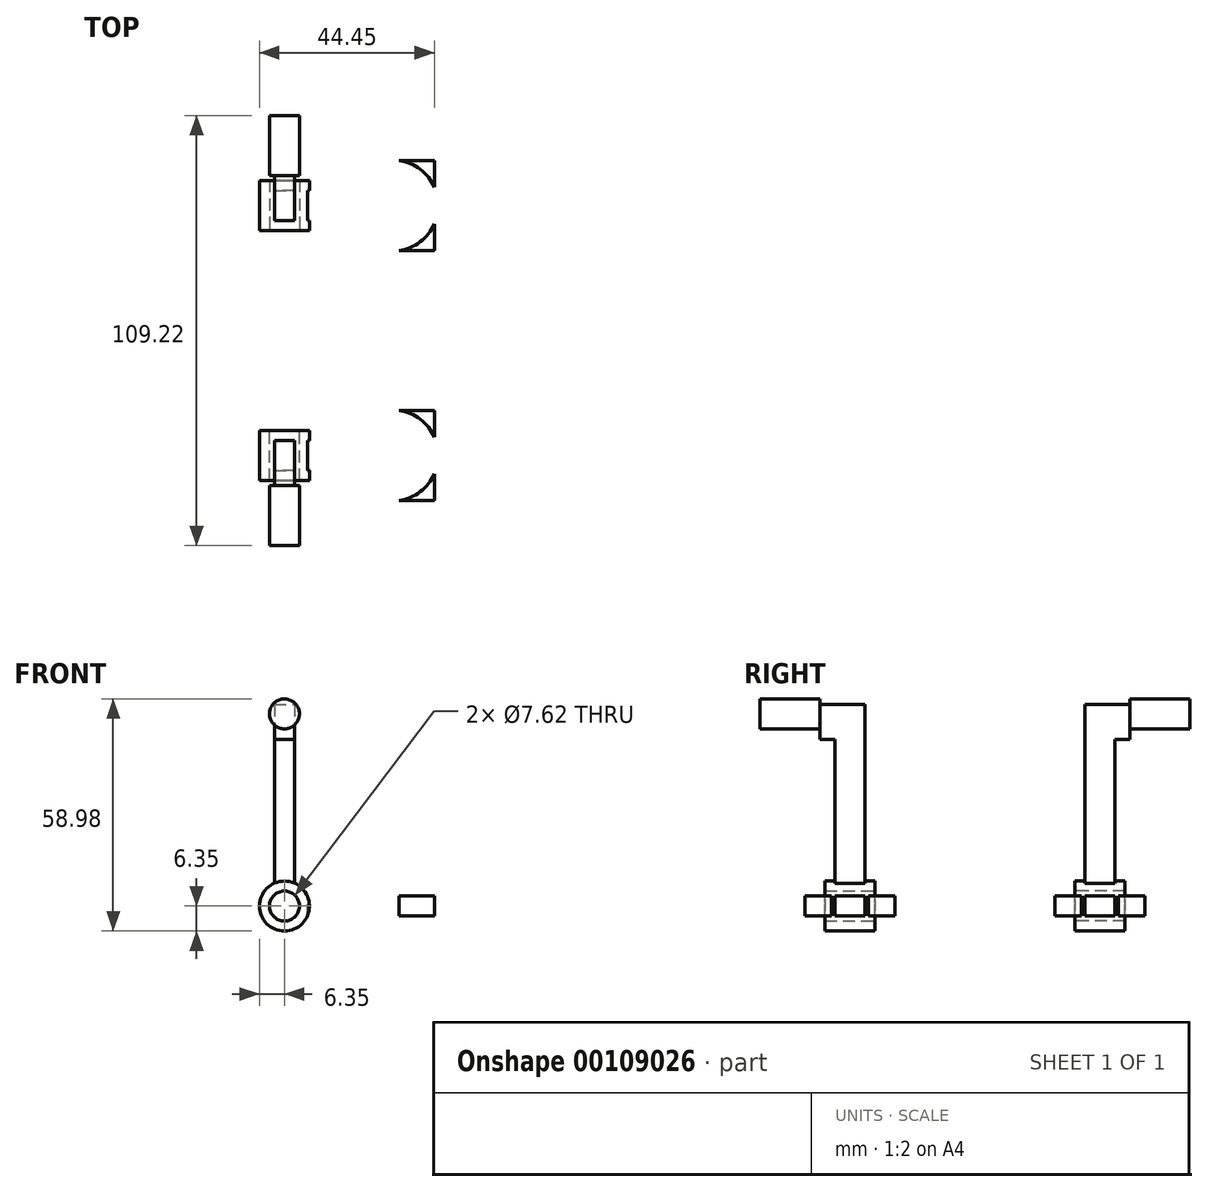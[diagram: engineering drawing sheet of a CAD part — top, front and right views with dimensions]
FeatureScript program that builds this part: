
annotation { "Feature Type Name" : "Feature", "Feature Type Description" : "" }
export const myFeature = defineFeature(function(context is Context, id is Id, definition is map)
    precondition{}
    {
        {
            var Q0;
            Q0=qCreatedBy(makeId("Front.planeOp"),FACE);
            var sketch = newSketch(context, id + "F0", { "sketchPlane" : qUnion([Q0])});
            skCircle(sketch, "E0", {"center": v(0, 0) * mm, "radius": 3.81 * mm});
            skCircle(sketch, "E1", {"center": v(0, 0) * mm, "radius": 6.35 * mm});
            skSolve(sketch);
        }
        {
            var Q0;
            Q0=makeQuery(id+"F0.imprint","IMPRINT",FACE,{"disambiguationData":[TD([[makeQuery(id+"F0.imprint","IMPRINT",EDGE,{"derivedFrom":sQuery(id+"F0.wireOp",EDGE,"E0")}),-1.0]])]});
            extrude(context, id + "F1", {"entities" : qUnion([Q0]), "depth" : 12.7 * mm});
        }
        {
            var Q0;
            Q0=qCreatedBy(makeId("Top.planeOp"),FACE);
            var sketch = newSketch(context, id + "F2", { "sketchPlane" : qUnion([Q0])});
            skLineSegment(sketch, "E2", {"start": v(0, 0) * mm, "end": v(-6.35, 0) * mm});
            skLineSegment(sketch, "E3", {"start": v(-6.35, -6.35) * mm, "end": v(-6.35, -10.16) * mm});
            skLineSegment(sketch, "E4", {"start": v(-6.35, -6.35) * mm, "end": v(-6.35, -2.54) * mm});
            skSolve(sketch);
        }
        {
            var Q0;
            Q0=qCreatedBy(makeId("Right.planeOp"),FACE);
            var sketch = newSketch(context, id + "F3", { "sketchPlane" : qUnion([Q0])});
            skLineSegment(sketch, "E5", {"start": v(-2.54, 0) * mm, "end": v(-2.54, 2.54) * mm});
            skLineSegment(sketch, "E6", {"start": v(-2.54, 0) * mm, "end": v(-2.54, -2.54) * mm});
            skLineSegment(sketch, "E7", {"start": v(-2.54, -2.54) * mm, "end": v(-10.16, -2.54) * mm});
            skLineSegment(sketch, "E8", {"start": v(-10.16, -2.54) * mm, "end": v(-10.16, 0) * mm});
            skLineSegment(sketch, "E9", {"start": v(-10.16, 0) * mm, "end": v(-10.16, 2.54) * mm});
            skLineSegment(sketch, "E10", {"start": v(-10.16, 2.54) * mm, "end": v(-2.54, 2.54) * mm});
            skSolve(sketch);
        }
        {
            var Q0;
            Q0=makeQuery(id+"F3.imprint","IMPRINT",FACE,{"disambiguationData":[TD([[makeQuery(id+"F3.imprint","IMPRINT",EDGE,{"derivedFrom":sQuery(id+"F3.wireOp",EDGE,"E5")}),1.0]])]});
            extrude(context, id + "F4", {"entities" : qUnion([Q0]), "operationType" : NewBodyOperationType.ADD, "depth" : 38.1 * mm});
        }
        {
            var Q0;
            Q0=makeQuery(id+"F0.imprint","IMPRINT",FACE,{"disambiguationData":[TD([[makeQuery(id+"F0.imprint","IMPRINT",EDGE,{"derivedFrom":sQuery(id+"F0.wireOp",EDGE,"E0")}),1.0]])]});
            extrude(context, id + "F5", {"entities" : qUnion([Q0]), "operationType" : NewBodyOperationType.REMOVE, "depth" : 25.4 * mm, "hasSecondDirection" : true, "secondDirectionOppositeDirection" : true, "secondDirectionDepth" : 25.4 * mm});
        }
        {
            var Q0;
            {var subQ1=sQuery(id+"F3.wireOp",EDGE,"E9");var subQ2=sQuery(id+"F3.wireOp",EDGE,"E8");Q0=makeQuery(id+"F4.boolean.opBoolean","SPLIT",FACE,{"disambiguationData":[TD([makeQuery(id+"F1.opExtrude","SWEPT_FACE",FACE,{"disambiguationData":[OSD([sQuery(id+"F0.wireOp",EDGE,"E1")])]})])],"derivedFrom":makeQuery(id+"F4.opExtrude","SWEPT_FACE",FACE,{"disambiguationData":[OSD([subQ2,subQ1])]})});}
            var sketch = newSketch(context, id + "F6", { "sketchPlane" : qUnion([Q0])});
            skLineSegment(sketch, "E11.bottom", {"start": v(24.28, 2.54) * mm, "end": v(38.1, 2.54) * mm});
            skLineSegment(sketch, "E11.top", {"start": v(24.28, -2.54) * mm, "end": v(38.1, -2.54) * mm});
            skLineSegment(sketch, "E11.left", {"start": v(24.28, 2.54) * mm, "end": v(24.28, -2.54) * mm});
            skLineSegment(sketch, "E11.right", {"start": v(38.1, 2.54) * mm, "end": v(38.1, -2.54) * mm});
            skSolve(sketch);
        }
        {
            var Q0;
            Q0=makeQuery(id+"F6.imprint","IMPRINT",FACE,{"disambiguationData":[TD([[makeQuery(id+"F6.imprint","IMPRINT",EDGE,{"derivedFrom":sQuery(id+"F6.wireOp",EDGE,"E11.bottom")}),1.0]])]});
            extrude(context, id + "F7", {"entities" : qUnion([Q0]), "operationType" : NewBodyOperationType.ADD, "depth" : 7.62 * mm, "hasSecondDirection" : true, "secondDirectionOppositeDirection" : true, "secondDirectionDepth" : 15.24 * mm});
        }
        {
            var Q0;
            {var subQ2=sQuery(id+"F6.wireOp",EDGE,"E11.left");Q0=makeQuery(id+"F7.boolean.opBoolean","SPLIT",FACE,{"disambiguationData":[TD([makeQuery(id+"F4.opExtrude","SWEPT_FACE",FACE,{"disambiguationData":[OSD([sQuery(id+"F3.wireOp",EDGE,"E8"),sQuery(id+"F3.wireOp",EDGE,"E9")])]})])],"derivedFrom":makeQuery(id+"F7.opExtrude","SWEPT_FACE",FACE,{"disambiguationData":[OSD([subQ2])]})});}
            extrude(context, id + "F8", {"entities" : qUnion([Q0]), "operationType" : NewBodyOperationType.ADD, "depth" : 7.62 * mm});
        }
        {
            var Q0;
            {var subQ1=sQuery(id+"F6.wireOp",EDGE,"E11.left");Q0=makeQuery(id+"F7.boolean.opBoolean","SPLIT",FACE,{"disambiguationData":[TD([makeQuery(id+"F4.opExtrude","SWEPT_FACE",FACE,{"disambiguationData":[OSD([sQuery(id+"F3.wireOp",EDGE,"E5"),sQuery(id+"F3.wireOp",EDGE,"E6")])]})])],"derivedFrom":makeQuery(id+"F7.opExtrude","SWEPT_FACE",FACE,{"disambiguationData":[OSD([subQ1])]})});}
            extrude(context, id + "F9", {"entities" : qUnion([Q0]), "operationType" : NewBodyOperationType.ADD, "depth" : 7.62 * mm});
        }
        {
            var Q0;
            {var subQ0=sQuery(id+"F6.wireOp",EDGE,"E11.left");var subQ1=sQuery(id+"F6.wireOp",EDGE,"E11.bottom");var subQ2=sQuery(id+"F3.wireOp",EDGE,"E10");var subQ3=sQuery(id+"F3.wireOp",EDGE,"E9");Q0=makeQuery(id+"F9.boolean.opBoolean","MERGE",FACE,{"derivedFrom":[makeQuery(id+"F8.boolean.opBoolean","MERGE",FACE,{"derivedFrom":[makeQuery(id+"F7.boolean.opBoolean","MERGE",FACE,{"derivedFrom":[makeQuery(id+"F4.boolean.opBoolean","SPLIT",FACE,{"disambiguationData":[TD([makeQuery(id+"F1.opExtrude","SWEPT_FACE",FACE,{"disambiguationData":[OSD([sQuery(id+"F0.wireOp",EDGE,"E1")])]})])],"derivedFrom":makeQuery(id+"F4.opExtrude","SWEPT_FACE",FACE,{"disambiguationData":[OSD([subQ2])]})}),makeQuery(id+"F7.opExtrude","SWEPT_FACE",FACE,{"disambiguationData":[OSD([subQ1])]})]}),makeQuery(id+"F8.opExtrude","SWEPT_FACE",FACE,{"disambiguationData":[OSD([subQ3,subQ2,subQ1,subQ0])]})]}),makeQuery(id+"F9.opExtrude","SWEPT_FACE",FACE,{"disambiguationData":[OSD([subQ3,subQ2,subQ1,subQ0])]})]});}
            var sketch = newSketch(context, id + "F10", { "sketchPlane" : qUnion([Q0])});
            skArc(sketch, "E12", {"start": v(16.66, -2.54) * mm, "mid": v(39.08, -6.35) * mm, "end": v(16.66, -10.16) * mm});
            skLineSegment(sketch, "E13", {"start": v(16.66, -2.54) * mm, "end": v(16.66, 5.08) * mm});
            skLineSegment(sketch, "E14", {"start": v(16.66, 5.08) * mm, "end": v(38.1, 5.08) * mm});
            skLineSegment(sketch, "E15", {"start": v(38.1, 5.08) * mm, "end": v(38.1, -17.78) * mm});
            skLineSegment(sketch, "E16", {"start": v(38.1, -17.78) * mm, "end": v(16.66, -17.78) * mm});
            skLineSegment(sketch, "E17", {"start": v(16.66, -17.78) * mm, "end": v(16.66, -10.16) * mm});
            skSolve(sketch);
        }
        {
            var Q0;
            {var subQ0=sQuery(id+"F10.wireOp",EDGE,"E17");Q0=makeQuery(id+"F10.imprint","IMPRINT",FACE,{"disambiguationData":[TD([[makeQuery(id+"F10.imprint","IMPRINT",EDGE,{"derivedFrom":subQ0}),-1.0]])]});}
            var Q1;
            {var subQ0=sQuery(id+"F10.wireOp",EDGE,"E13");Q1=makeQuery(id+"F10.imprint","IMPRINT",FACE,{"disambiguationData":[TD([[makeQuery(id+"F10.imprint","IMPRINT",EDGE,{"derivedFrom":subQ0}),-1.0]])]});}
            var Q2;
            {var subQ0=sQuery(id+"F10.wireOp",EDGE,"E14");var subQ1=sQuery(id+"F10.wireOp",EDGE,"E12");var subQ2=makeQuery(id+"F10.imprint","INTERSECT",VERTEX,{"disambiguationData":[OD(1.0)],"derivedFrom":[subQ1,subQ0]});Q2=makeQuery(id+"F10.imprint","IMPRINT",FACE,{"disambiguationData":[TD([[makeQuery(id+"F10.imprint","IMPRINT",EDGE,{"disambiguationData":[TD([[subQ2,-1.0]])],"derivedFrom":subQ1}),1.0]])]});}
            var Q3;
            {var subQ0=sQuery(id+"F10.wireOp",EDGE,"E15");var subQ1=sQuery(id+"F10.wireOp",EDGE,"E12");var subQ2=makeQuery(id+"F10.imprint","INTERSECT",VERTEX,{"disambiguationData":[OD(1.0)],"derivedFrom":[subQ1,subQ0]});Q3=makeQuery(id+"F10.imprint","IMPRINT",FACE,{"disambiguationData":[TD([[makeQuery(id+"F10.imprint","IMPRINT",EDGE,{"disambiguationData":[TD([[subQ2,-1.0]])],"derivedFrom":subQ1}),1.0]])]});}
            extrude(context, id + "F11", {"entities" : qUnion([Q0, Q1, Q2, Q3]), "operationType" : NewBodyOperationType.REMOVE, "oppositeDirection" : true, "depth" : 25.4 * mm});
        }
        {
            var Q0;
            {var subQ0=sQuery(id+"F10.wireOp",EDGE,"E15");var subQ1=sQuery(id+"F10.wireOp",EDGE,"E12");var subQ2=makeQuery(id+"F10.imprint","INTERSECT",VERTEX,{"disambiguationData":[OD(0.0)],"derivedFrom":[subQ1,subQ0]});Q0=makeQuery(id+"F10.imprint","IMPRINT",FACE,{"disambiguationData":[TD([[makeQuery(id+"F10.imprint","IMPRINT",EDGE,{"disambiguationData":[TD([[subQ2,-1.0]])],"derivedFrom":subQ1}),-1.0]])]});}
            extrude(context, id + "F12", {"entities" : qUnion([Q0]), "operationType" : NewBodyOperationType.ADD, "oppositeDirection" : true, "depth" : 5.08 * mm});
        }
        {
            var Q0;
            Q0=qCreatedBy(makeId("Top.planeOp"),FACE);
            var sketch = newSketch(context, id + "F13", { "sketchPlane" : qUnion([Q0])});
            skLineSegment(sketch, "E18", {"start": v(0, -2.54) * mm, "end": v(-2.54, -2.54) * mm});
            skLineSegment(sketch, "E19", {"start": v(0, -2.54) * mm, "end": v(2.54, -2.54) * mm});
            skLineSegment(sketch, "E20", {"start": v(2.54, -2.54) * mm, "end": v(2.54, -10.16) * mm});
            skLineSegment(sketch, "E21", {"start": v(-2.54, -2.54) * mm, "end": v(-2.54, -10.16) * mm});
            skLineSegment(sketch, "E22", {"start": v(-2.54, -10.16) * mm, "end": v(0, -10.16) * mm});
            skLineSegment(sketch, "E23", {"start": v(0, -10.16) * mm, "end": v(2.54, -10.16) * mm});
            skSolve(sketch);
        }
        {
            var Q0;
            Q0=makeQuery(id+"F13.imprint","IMPRINT",FACE,{"disambiguationData":[TD([[makeQuery(id+"F13.imprint","IMPRINT",EDGE,{"derivedFrom":sQuery(id+"F13.wireOp",EDGE,"E18")}),1.0]])]});
            extrude(context, id + "F14", {"entities" : qUnion([Q0]), "operationType" : NewBodyOperationType.ADD, "depth" : 51.23 * mm});
        }
        {
            var Q0;
            Q0=makeQuery(id+"F0.imprint","IMPRINT",FACE,{"disambiguationData":[TD([[makeQuery(id+"F0.imprint","IMPRINT",EDGE,{"derivedFrom":sQuery(id+"F0.wireOp",EDGE,"E0")}),1.0]])]});
            extrude(context, id + "F15", {"entities" : qUnion([Q0]), "operationType" : NewBodyOperationType.REMOVE, "depth" : 25.4 * mm});
        }
        {
            var Q0;
            {var subQ0=sQuery(id+"F13.wireOp",EDGE,"E23");var subQ1=sQuery(id+"F13.wireOp",EDGE,"E22");Q0=makeQuery(id+"F14.boolean.opBoolean","SPLIT",FACE,{"disambiguationData":[TD([makeQuery(id+"F1.opExtrude","SWEPT_FACE",FACE,{"disambiguationData":[OSD([sQuery(id+"F0.wireOp",EDGE,"E1")])]})])],"derivedFrom":makeQuery(id+"F14.opExtrude","SWEPT_FACE",FACE,{"disambiguationData":[OSD([subQ1,subQ0])]})});}
            var sketch = newSketch(context, id + "F16", { "sketchPlane" : qUnion([Q0])});
            skLineSegment(sketch, "E24", {"start": v(0, 51.23) * mm, "end": v(0, 42.34) * mm});
            skPoint(sketch, "E24.endSnap0", {"position": v(0, 51.23) * mm});
            skLineSegment(sketch, "E25", {"start": v(0, 42.34) * mm, "end": v(2.54, 42.34) * mm});
            skLineSegment(sketch, "E26", {"start": v(0, 42.34) * mm, "end": v(-2.54, 42.34) * mm});
            skSolve(sketch);
        }
        {
            var Q0;
            {var subQ0=sQuery(id+"F16.wireOp",EDGE,"E24");Q0=makeQuery(id+"F16.imprint","IMPRINT",FACE,{"disambiguationData":[TD([[makeQuery(id+"F16.imprint","IMPRINT",EDGE,{"derivedFrom":subQ0}),-1.0]])]});}
            var Q1;
            {var subQ0=sQuery(id+"F16.wireOp",EDGE,"E24");Q1=makeQuery(id+"F16.imprint","IMPRINT",FACE,{"disambiguationData":[TD([[makeQuery(id+"F16.imprint","IMPRINT",EDGE,{"derivedFrom":subQ0}),1.0]])]});}
            extrude(context, id + "F17", {"entities" : qUnion([Q0, Q1]), "operationType" : NewBodyOperationType.ADD, "depth" : 11.43 * mm});
        }
        {
            var Q0;
            Q0=makeQuery(id+"F17.opExtrude","CAP_FACE",FACE,{"disambiguationData":[OSD([sQuery(id+"F13.wireOp",EDGE,"E20"),sQuery(id+"F13.wireOp",EDGE,"E21"),sQuery(id+"F13.wireOp",EDGE,"E22"),sQuery(id+"F13.wireOp",EDGE,"E23"),sQuery(id+"F16.wireOp",EDGE,"E25"),sQuery(id+"F16.wireOp",EDGE,"E26")])],"isStart":false});
            var sketch = newSketch(context, id + "F18", { "sketchPlane" : qUnion([Q0])});
            skCircle(sketch, "E27", {"center": v(0, 48.82) * mm, "radius": 3.81 * mm});
            skCircle(sketch, "E28", {"center": v(0, 48.82) * mm, "radius": 6.35 * mm});
            skLineSegment(sketch, "E29", {"start": v(0, 0) * mm, "end": v(0, 48.82) * mm});
            skSolve(sketch);
        }
        {
            var Q0;
            {var subQ1=sQuery(id+"F13.wireOp",EDGE,"E23");var subQ4=sQuery(id+"F13.wireOp",EDGE,"E22");var subQ7=makeQuery(id+"F17.opExtrude","CAP_EDGE",EDGE,{"disambiguationData":[OSD([subQ4,subQ1])],"isStart":false});Q0=makeQuery(id+"F18.imprint","IMPRINT",FACE,{"disambiguationData":[TD([[makeQuery(id+"F18.imprint","IMPRINT",EDGE,{"derivedFrom":subQ7}),1.0]])]});}
            var Q1;
            {var subQ1=sQuery(id+"F13.wireOp",EDGE,"E23");var subQ4=sQuery(id+"F13.wireOp",EDGE,"E22");var subQ7=makeQuery(id+"F17.opExtrude","CAP_EDGE",EDGE,{"disambiguationData":[OSD([subQ4,subQ1])],"isStart":false});Q1=makeQuery(id+"F18.imprint","IMPRINT",FACE,{"disambiguationData":[TD([[makeQuery(id+"F18.imprint","IMPRINT",EDGE,{"derivedFrom":subQ7}),-1.0]])]});}
            extrude(context, id + "F19", {"entities" : qUnion([Q0, Q1]), "operationType" : NewBodyOperationType.ADD, "depth" : 7.62 * mm, "hasSecondDirection" : true, "secondDirectionOppositeDirection" : true, "secondDirectionDepth" : 7.62 * mm});
        }
        {
            var Q0;
            Q0=makeQuery(id+"F17.opExtrude","CAP_FACE",FACE,{"disambiguationData":[OSD([sQuery(id+"F13.wireOp",EDGE,"E20"),sQuery(id+"F13.wireOp",EDGE,"E21"),sQuery(id+"F13.wireOp",EDGE,"E22"),sQuery(id+"F13.wireOp",EDGE,"E23"),sQuery(id+"F16.wireOp",EDGE,"E25"),sQuery(id+"F16.wireOp",EDGE,"E26")])],"isStart":false});
            extrude(context, id + "F20", {"entities" : qUnion([Q0]), "operationType" : NewBodyOperationType.REMOVE, "oppositeDirection" : true, "depth" : 7.62 * mm});
        }
        {
            var Q0;
            Q0=qCreatedBy(makeId("Front.planeOp"),FACE);
            cPlane(context, id + "F21", {"entities" : qUnion([Q0]), "cplaneType" : CPlaneType.OFFSET, "offset" : 25.4 * mm, "oppositeDirection" : true, "width" : 152.4 * mm, "height" : 152.4 * mm});
        }
        {
            var Q0;
            Q0=makeQuery(id+"F1.opExtrude","SWEPT_BODY",BODY,{"disambiguationData":[OSD([sQuery(id+"F0.wireOp",EDGE,"E0"),sQuery(id+"F0.wireOp",EDGE,"E1")])]});
            var Q1;
            Q1=qCreatedBy(id+"F21.planeOp",FACE);
            mirror(context, id + "F22", {"entities" : qUnion([Q0]), "mirrorPlane" : qUnion([Q1])});
        }
    });
